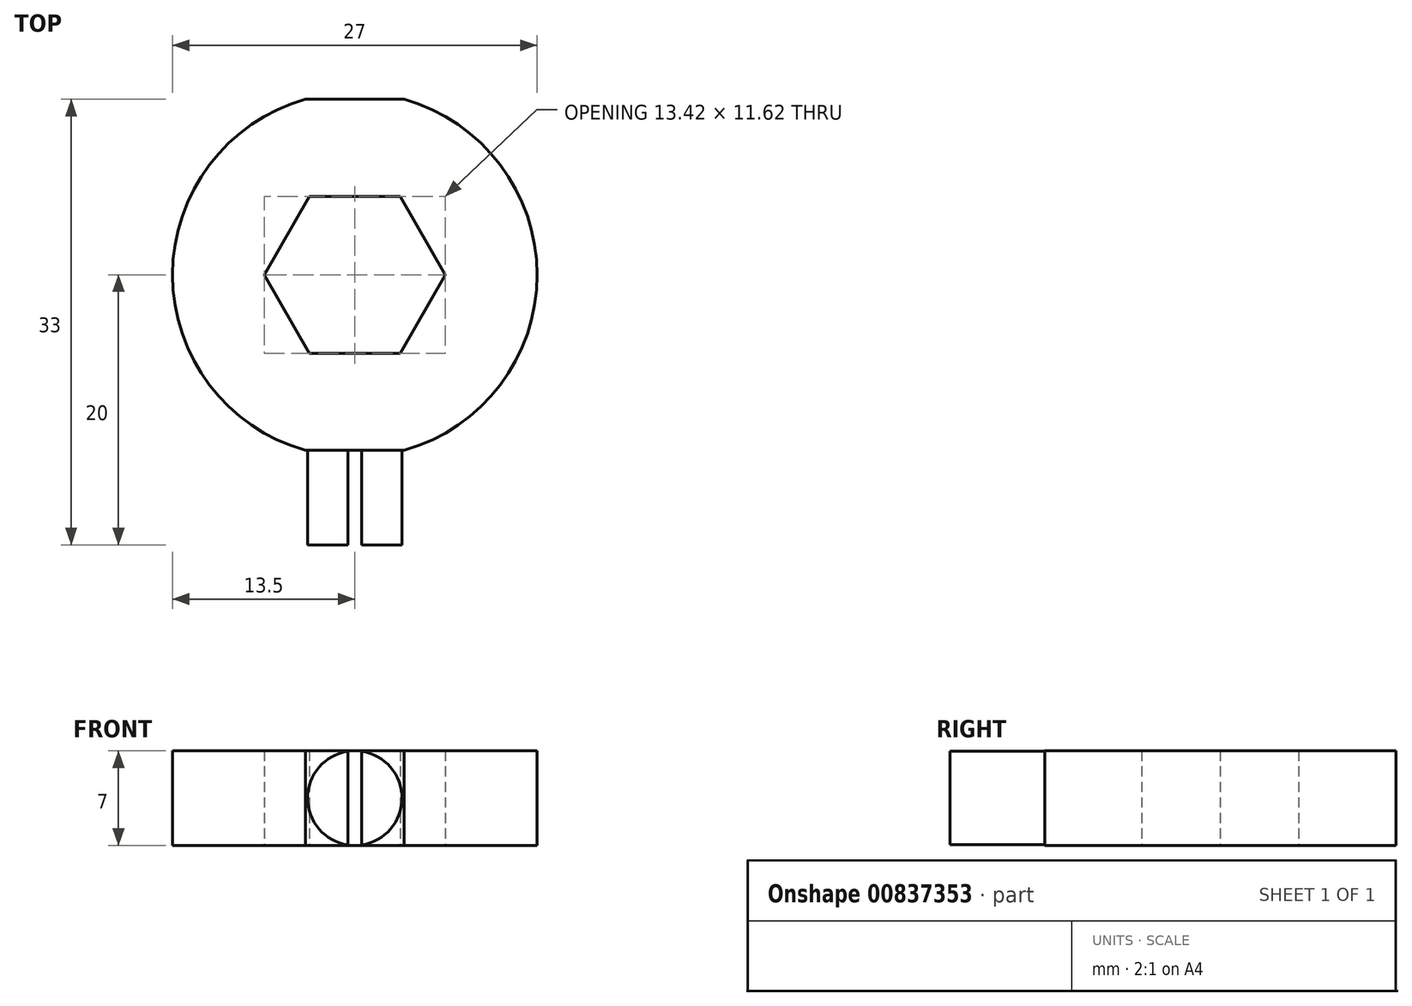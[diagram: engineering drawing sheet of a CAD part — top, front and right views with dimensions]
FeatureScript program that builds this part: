
annotation { "Feature Type Name" : "Feature", "Feature Type Description" : "" }
export const myFeature = defineFeature(function(context is Context, id is Id, definition is map)
    precondition{}
    {
        {
            var Q0;
            Q0=qCreatedBy(makeId("Top.planeOp"),FACE);
            var sketch = newSketch(context, id + "F0", { "sketchPlane" : qUnion([Q0])});
            skArc(sketch, "E0", {"start": v(-3.64, 13) * mm, "mid": v(-13.5, 0) * mm, "end": v(-3.64, -13) * mm});
            skLineSegment(sketch, "E1", {"start": v(-3.64, 13) * mm, "end": v(3.64, 13) * mm});
            skLineSegment(sketch, "E2", {"start": v(-3.64, -13) * mm, "end": v(3.64, -13) * mm});
            skArc(sketch, "E3.trimOffspring", {"start": v(3.64, -13) * mm, "mid": v(13.5, 0) * mm, "end": v(3.64, 13) * mm});
            skCircle(sketch, "E4", {"center": v(0, 0) * mm, "radius": 6.7 * mm, "construction": true});
            skLineSegment(sketch, "E5", {"start": v(-3.35, 5.81) * mm, "end": v(3.35, 5.81) * mm});
            skLineSegment(sketch, "E6", {"start": v(3.35, 5.81) * mm, "end": v(6.7, 0) * mm});
            skLineSegment(sketch, "E7", {"start": v(6.7, 0) * mm, "end": v(3.35, -5.81) * mm});
            skLineSegment(sketch, "E8", {"start": v(3.35, -5.81) * mm, "end": v(-3.35, -5.81) * mm});
            skLineSegment(sketch, "E9", {"start": v(-3.35, -5.81) * mm, "end": v(-6.7, 0) * mm});
            skLineSegment(sketch, "E10", {"start": v(-6.7, 0) * mm, "end": v(-3.35, 5.81) * mm});
            skSolve(sketch);
        }
        {
            var Q0;
            Q0=makeQuery(id+"F0.imprint","IMPRINT",FACE,{"disambiguationData":[TD([[makeQuery(id+"F0.imprint","IMPRINT",EDGE,{"derivedFrom":sQuery(id+"F0.wireOp",EDGE,"E0")}),1.0]])]});
            extrude(context, id + "F1", {"entities" : qUnion([Q0]), "depth" : 7 * mm, "offsetDistance" : 25 * mm});
        }
        {
            var Q0;
            Q0=makeQuery(id+"F1.opExtrude","SWEPT_FACE",FACE,{"disambiguationData":[OSD([sQuery(id+"F0.wireOp",EDGE,"E2")])]});
            var sketch = newSketch(context, id + "F2", { "sketchPlane" : qUnion([Q0])});
            skLineSegment(sketch, "E11", {"start": v(-3.64, 7) * mm, "end": v(3.64, 0) * mm, "construction": true});
            skLineSegment(sketch, "E12", {"start": v(-3.64, 0) * mm, "end": v(3.64, 7) * mm, "construction": true});
            skCircle(sketch, "E13", {"center": v(0, 3.5) * mm, "radius": 3.5 * mm});
            skLineSegment(sketch, "E14", {"start": v(-0.5, 6.96) * mm, "end": v(-0.5, 0.04) * mm});
            skLineSegment(sketch, "E15", {"start": v(0.5, 6.96) * mm, "end": v(0.5, 0.04) * mm});
            skSolve(sketch);
        }
        {
            var Q0;
            {var subQ0=sQuery(id+"F2.wireOp",EDGE,"E14");Q0=makeQuery(id+"F2.imprint","IMPRINT",FACE,{"disambiguationData":[TD([[makeQuery(id+"F2.imprint","IMPRINT",EDGE,{"derivedFrom":subQ0}),-1.0]])]});}
            var Q1;
            {var subQ0=sQuery(id+"F2.wireOp",EDGE,"E15");Q1=makeQuery(id+"F2.imprint","IMPRINT",FACE,{"disambiguationData":[TD([[makeQuery(id+"F2.imprint","IMPRINT",EDGE,{"derivedFrom":subQ0}),1.0]])]});}
            extrude(context, id + "F3", {"entities" : qUnion([Q0, Q1]), "operationType" : NewBodyOperationType.ADD, "depth" : 7 * mm, "offsetDistance" : 25 * mm});
        }
    });
